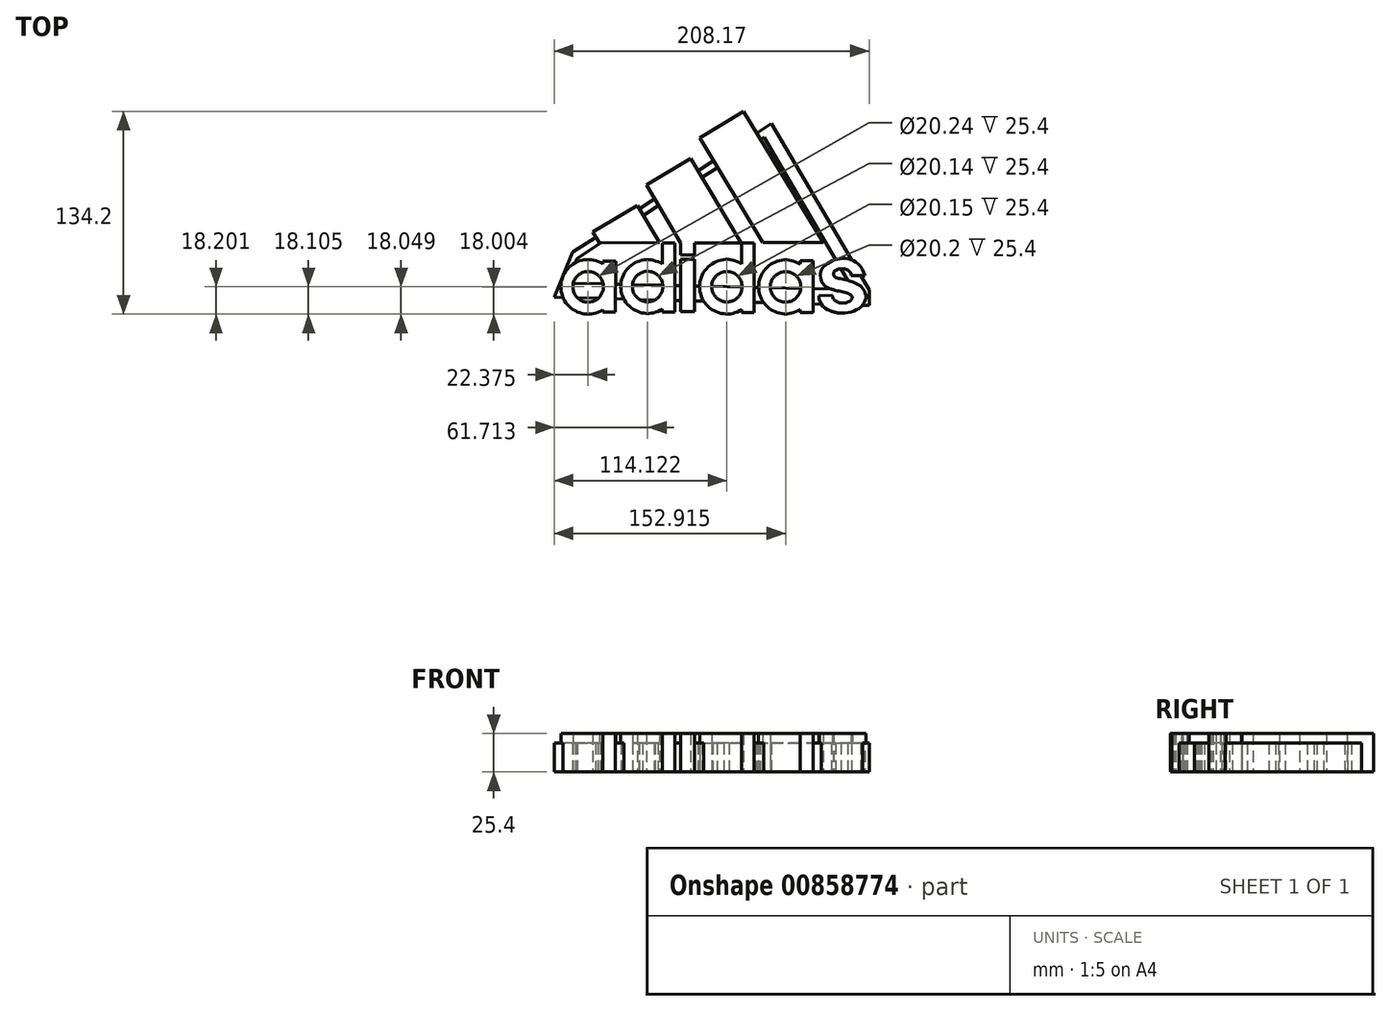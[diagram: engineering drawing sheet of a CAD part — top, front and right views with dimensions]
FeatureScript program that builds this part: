
annotation { "Feature Type Name" : "Feature", "Feature Type Description" : "" }
export const myFeature = defineFeature(function(context is Context, id is Id, definition is map)
    precondition{}
    {
        {
            var Q0;
            Q0=qCreatedBy(makeId("Top.planeOp"),FACE);
            var sketch = newSketch(context, id + "F0", { "sketchPlane" : qUnion([Q0])});
            skLineSegment(sketch, "E0", {"start": v(-108.73, -20.06) * mm, "end": v(-104.25, -27.54) * mm});
            skLineSegment(sketch, "E1", {"start": v(-64.76, -27.2) * mm, "end": v(-104.25, -27.54) * mm});
            skLineSegment(sketch, "E2", {"start": v(-108.73, -20.06) * mm, "end": v(-79.42, -2.53) * mm});
            skLineSegment(sketch, "E3", {"start": v(-79.42, -2.53) * mm, "end": v(-64.76, -27.2) * mm});
            skLineSegment(sketch, "E4", {"start": v(-73.41, 10.93) * mm, "end": v(-50.58, -27.49) * mm});
            skLineSegment(sketch, "E5", {"start": v(-50.58, -27.49) * mm, "end": v(-10.72, -27.49) * mm});
            skLineSegment(sketch, "E6", {"start": v(-10.72, -27.49) * mm, "end": v(-43.97, 28.43) * mm});
            skLineSegment(sketch, "E7", {"start": v(-43.97, 28.43) * mm, "end": v(-73.41, 10.93) * mm});
            skLineSegment(sketch, "E8", {"start": v(-38.16, 42.1) * mm, "end": v(3.67, -27.23) * mm});
            skLineSegment(sketch, "E9", {"start": v(-38.16, 42.1) * mm, "end": v(-8.99, 59.7) * mm});
            skLineSegment(sketch, "E10", {"start": v(-8.99, 59.7) * mm, "end": v(43.48, -27.26) * mm});
            skLineSegment(sketch, "E11", {"start": v(43.48, -27.26) * mm, "end": v(3.67, -27.23) * mm});
            skCircle(sketch, "E12", {"center": v(-111.85, -56.45) * mm, "radius": 10.12 * mm});
            skCircle(sketch, "E13", {"center": v(-111.85, -56.45) * mm, "radius": 18.05 * mm});
            skLineSegment(sketch, "E14", {"start": v(-102.06, -39.5) * mm, "end": v(-102.06, -73.1) * mm});
            skLineSegment(sketch, "E15", {"start": v(-102.06, -73.1) * mm, "end": v(-93.82, -73.1) * mm});
            skLineSegment(sketch, "E16", {"start": v(-102.06, -39.5) * mm, "end": v(-93.69, -39.5) * mm});
            skLineSegment(sketch, "E17", {"start": v(-93.69, -39.5) * mm, "end": v(-93.82, -73.1) * mm});
            skLineSegment(sketch, "E18.bottom", {"start": v(-62.74, -27.53) * mm, "end": v(-54.5, -27.53) * mm});
            skLineSegment(sketch, "E18.top", {"start": v(-62.74, -73.26) * mm, "end": v(-54.5, -73.26) * mm});
            skLineSegment(sketch, "E18.left", {"start": v(-62.74, -27.53) * mm, "end": v(-62.74, -73.26) * mm});
            skLineSegment(sketch, "E18.right", {"start": v(-54.5, -27.53) * mm, "end": v(-54.5, -73.26) * mm});
            skCircle(sketch, "E19", {"center": v(-72.52, -56.3) * mm, "radius": 10.07 * mm});
            skPoint(sketch, "E19.centerSnap0", {"position": v(-93.76, -56.3) * mm});
            skCircle(sketch, "E20", {"center": v(-72.52, -56.3) * mm, "radius": 17.78 * mm});
            skLineSegment(sketch, "E21.bottom", {"start": v(-41.5, -35.39) * mm, "end": v(-50.58, -35.39) * mm});
            skLineSegment(sketch, "E21.top", {"start": v(-41.5, -27.49) * mm, "end": v(-50.58, -27.49) * mm});
            skLineSegment(sketch, "E21.left", {"start": v(-41.5, -35.39) * mm, "end": v(-41.5, -27.49) * mm});
            skLineSegment(sketch, "E21.right", {"start": v(-50.58, -35.39) * mm, "end": v(-50.58, -27.49) * mm});
            skLineSegment(sketch, "E22.bottom", {"start": v(-41.5, -72.88) * mm, "end": v(-50.58, -72.88) * mm});
            skLineSegment(sketch, "E22.top", {"start": v(-41.5, -38.2) * mm, "end": v(-50.58, -38.2) * mm});
            skLineSegment(sketch, "E22.left", {"start": v(-41.5, -72.88) * mm, "end": v(-41.5, -38.2) * mm});
            skLineSegment(sketch, "E22.right", {"start": v(-50.58, -72.88) * mm, "end": v(-50.58, -38.2) * mm});
            skCircle(sketch, "E23", {"center": v(-20.1, -56.4) * mm, "radius": 10.07 * mm});
            skCircle(sketch, "E24", {"center": v(-20.1, -56.4) * mm, "radius": 18.03 * mm});
            skLineSegment(sketch, "E25.bottom", {"start": v(-2.09, -27.49) * mm, "end": v(-10.23, -27.49) * mm});
            skLineSegment(sketch, "E25.top", {"start": v(-2.09, -73.45) * mm, "end": v(-10.23, -73.45) * mm});
            skLineSegment(sketch, "E25.left", {"start": v(-2.09, -27.49) * mm, "end": v(-2.09, -73.45) * mm});
            skLineSegment(sketch, "E25.right", {"start": v(-10.23, -27.49) * mm, "end": v(-10.23, -73.45) * mm});
            skCircle(sketch, "E26", {"center": v(18.68, -56.5) * mm, "radius": 10.1 * mm});
            skCircle(sketch, "E27", {"center": v(18.68, -56.5) * mm, "radius": 17.84 * mm});
            skLineSegment(sketch, "E28.bottom", {"start": v(36.83, -39.32) * mm, "end": v(28.43, -39.32) * mm});
            skLineSegment(sketch, "E28.top", {"start": v(36.83, -73.47) * mm, "end": v(28.43, -73.47) * mm});
            skLineSegment(sketch, "E28.left", {"start": v(36.83, -39.32) * mm, "end": v(36.83, -73.47) * mm});
            skLineSegment(sketch, "E28.right", {"start": v(28.43, -39.32) * mm, "end": v(28.43, -73.47) * mm});
            skFitSpline(sketch, "E29", {"points": [v(40.61, -62.28) * mm, v(71.7, -62.17) * mm], "startDerivative": vector(1.62, -49.72) * mm, "endDerivative": vector(-4.39, 42.82) * mm});
            skFitSpline(sketch, "E30", {"points": [v(71.7, -62.17) * mm, v(50.6, -47.52) * mm], "startDerivative": vector(-6.03, 39.02) * mm, "endDerivative": vector(7.86, 17.11) * mm});
            skFitSpline(sketch, "E31", {"points": [v(50.6, -47.52) * mm, v(62.11, -49.02) * mm], "startDerivative": vector(-5.58, 6.43) * mm, "endDerivative": vector(4.14, -23.75) * mm});
            skFitSpline(sketch, "E32", {"points": [v(71.08, -49.17) * mm, v(41.72, -49.17) * mm], "startDerivative": vector(-16, 60.18) * mm, "endDerivative": vector(5.1, -29.55) * mm});
            skFitSpline(sketch, "E33", {"points": [v(41.72, -49.17) * mm, v(62.92, -63.95) * mm], "startDerivative": vector(1.36, -39.32) * mm, "endDerivative": vector(3.01, -20.74) * mm});
            skFitSpline(sketch, "E34", {"points": [v(62.92, -63.95) * mm, v(49.69, -61.97) * mm], "startDerivative": vector(-10.24, -16.5) * mm, "endDerivative": vector(1, 16.73) * mm});
            skLineSegment(sketch, "E35", {"start": v(40.61, -62.28) * mm, "end": v(49.69, -61.97) * mm});
            skLineSegment(sketch, "E36", {"start": v(62.11, -49.02) * mm, "end": v(71.08, -49.17) * mm});
            skSolve(sketch);
        }
        {
            var Q0;
            Q0=qCreatedBy(makeId("Top.planeOp"),FACE);
            var sketch = newSketch(context, id + "F1", { "sketchPlane" : qUnion([Q0])});
            skLineSegment(sketch, "E37", {"start": v(-122.16, -33.53) * mm, "end": v(9.42, 51.78) * mm});
            skLineSegment(sketch, "E38", {"start": v(9.42, 51.78) * mm, "end": v(73.94, -58.57) * mm});
            skLineSegment(sketch, "E39", {"start": v(73.94, -58.57) * mm, "end": v(73.94, -68.76) * mm});
            skLineSegment(sketch, "E40", {"start": v(73.94, -68.76) * mm, "end": v(-134.23, -63.34) * mm});
            skLineSegment(sketch, "E41", {"start": v(-134.23, -63.34) * mm, "end": v(-122.16, -33.53) * mm});
            skLineSegment(sketch, "E42", {"start": v(-122.16, -33.53) * mm, "end": v(-119.4, -37.78) * mm});
            skLineSegment(sketch, "E43", {"start": v(-119.4, -37.78) * mm, "end": v(-128.2, -63.5) * mm});
            skPoint(sketch, "E43.endSnap0", {"position": v(-128.2, -48.44) * mm});
            skLineSegment(sketch, "E44", {"start": v(-119.4, -37.78) * mm, "end": v(11.98, 47.41) * mm});
            skLineSegment(sketch, "E45", {"start": v(73.94, -58.57) * mm, "end": v(-124.94, -53.97) * mm});
            skLineSegment(sketch, "E46", {"start": v(63.3, -58.33) * mm, "end": v(4.37, 42.48) * mm});
            skSolve(sketch);
        }
        {
            var Q0;
            Q0=makeQuery(id+"F0.imprint","IMPRINT",FACE,{"disambiguationData":[TD([[makeQuery(id+"F0.imprint","IMPRINT",EDGE,{"derivedFrom":sQuery(id+"F0.wireOp",EDGE,"E4")}),1.0]])]});
            var Q1;
            Q1=makeQuery(id+"F0.imprint","IMPRINT",FACE,{"disambiguationData":[TD([[makeQuery(id+"F0.imprint","IMPRINT",EDGE,{"derivedFrom":sQuery(id+"F0.wireOp",EDGE,"E8")}),1.0]])]});
            var Q2;
            Q2=makeQuery(id+"F0.imprint","IMPRINT",FACE,{"disambiguationData":[TD([[makeQuery(id+"F0.imprint","IMPRINT",EDGE,{"derivedFrom":sQuery(id+"F0.wireOp",EDGE,"E0")}),1.0]])]});
            var Q3;
            {var subQ0=sQuery(id+"F0.wireOp",EDGE,"E14");var subQ1=sQuery(id+"F0.wireOp",EDGE,"E12");var subQ2=makeQuery(id+"F0.imprint","INTERSECT",VERTEX,{"disambiguationData":[OD(0.0)],"derivedFrom":[subQ1,subQ0]});Q3=makeQuery(id+"F0.imprint","IMPRINT",FACE,{"disambiguationData":[TD([[makeQuery(id+"F0.imprint","IMPRINT",EDGE,{"disambiguationData":[TD([[subQ2,-1.0]])],"derivedFrom":subQ1}),-1.0]])]});}
            var Q4;
            {var subQ0=sQuery(id+"F0.wireOp",EDGE,"E14");var subQ1=sQuery(id+"F0.wireOp",EDGE,"E12");var subQ2=makeQuery(id+"F0.imprint","INTERSECT",VERTEX,{"disambiguationData":[OD(0.0)],"derivedFrom":[subQ1,subQ0]});Q4=makeQuery(id+"F0.imprint","IMPRINT",FACE,{"disambiguationData":[TD([[makeQuery(id+"F0.imprint","IMPRINT",EDGE,{"disambiguationData":[TD([[subQ2,1.0]])],"derivedFrom":subQ1}),-1.0]])]});}
            var Q5;
            {var subQ0=sQuery(id+"F0.wireOp",EDGE,"E20");var subQ1=sQuery(id+"F0.wireOp",EDGE,"E18.left");var subQ2=makeQuery(id+"F0.imprint","INTERSECT",VERTEX,{"disambiguationData":[OD(0.0)],"derivedFrom":[subQ1,subQ0]});Q5=makeQuery(id+"F0.imprint","IMPRINT",FACE,{"disambiguationData":[TD([[makeQuery(id+"F0.imprint","IMPRINT",EDGE,{"disambiguationData":[TD([[subQ2,-1.0]])],"derivedFrom":subQ1}),1.0]])]});}
            var Q6;
            {var subQ0=sQuery(id+"F0.wireOp",EDGE,"E20");var subQ1=sQuery(id+"F0.wireOp",EDGE,"E18.left");var subQ2=makeQuery(id+"F0.imprint","INTERSECT",VERTEX,{"disambiguationData":[OD(0.0)],"derivedFrom":[subQ1,subQ0]});Q6=makeQuery(id+"F0.imprint","IMPRINT",FACE,{"disambiguationData":[TD([[makeQuery(id+"F0.imprint","IMPRINT",EDGE,{"disambiguationData":[TD([[subQ2,-1.0]])],"derivedFrom":subQ1}),-1.0]])]});}
            var Q7;
            {var subQ1=sQuery(id+"F0.wireOp",EDGE,"E18.bottom");Q7=makeQuery(id+"F0.imprint","IMPRINT",FACE,{"disambiguationData":[TD([[makeQuery(id+"F0.imprint","IMPRINT",EDGE,{"derivedFrom":subQ1}),-1.0]])]});}
            var Q8;
            Q8=makeQuery(id+"F0.imprint","IMPRINT",FACE,{"disambiguationData":[TD([[makeQuery(id+"F0.imprint","IMPRINT",EDGE,{"derivedFrom":sQuery(id+"F0.wireOp",EDGE,"E22.bottom")}),-1.0]])]});
            var Q9;
            Q9=makeQuery(id+"F0.imprint","IMPRINT",FACE,{"disambiguationData":[TD([[makeQuery(id+"F0.imprint","IMPRINT",EDGE,{"derivedFrom":sQuery(id+"F0.wireOp",EDGE,"E21.bottom")}),-1.0]])]});
            var Q10;
            {var subQ0=sQuery(id+"F0.wireOp",EDGE,"E25.right");var subQ1=sQuery(id+"F0.wireOp",EDGE,"E23");var subQ2=makeQuery(id+"F0.imprint","INTERSECT",VERTEX,{"disambiguationData":[OD(0.0)],"derivedFrom":[subQ1,subQ0]});Q10=makeQuery(id+"F0.imprint","IMPRINT",FACE,{"disambiguationData":[TD([[makeQuery(id+"F0.imprint","IMPRINT",EDGE,{"disambiguationData":[TD([[subQ2,-1.0]])],"derivedFrom":subQ1}),-1.0]])]});}
            var Q11;
            {var subQ4=sQuery(id+"F0.wireOp",EDGE,"E25.right");var subQ7=sQuery(id+"F0.wireOp",EDGE,"E23");var subQ8=makeQuery(id+"F0.imprint","INTERSECT",VERTEX,{"disambiguationData":[OD(0.0)],"derivedFrom":[subQ7,subQ4]});Q11=makeQuery(id+"F0.imprint","IMPRINT",FACE,{"disambiguationData":[TD([[makeQuery(id+"F0.imprint","IMPRINT",EDGE,{"disambiguationData":[TD([[subQ8,1.0]])],"derivedFrom":subQ7}),-1.0]])]});}
            var Q12;
            {var subQ5=sQuery(id+"F0.wireOp",EDGE,"E25.bottom");Q12=makeQuery(id+"F0.imprint","IMPRINT",FACE,{"disambiguationData":[TD([[makeQuery(id+"F0.imprint","IMPRINT",EDGE,{"derivedFrom":subQ5}),1.0]])]});}
            var Q13;
            {var subQ5=sQuery(id+"F0.wireOp",EDGE,"E25.top");Q13=makeQuery(id+"F0.imprint","IMPRINT",FACE,{"disambiguationData":[TD([[makeQuery(id+"F0.imprint","IMPRINT",EDGE,{"derivedFrom":subQ5}),-1.0]])]});}
            var Q14;
            {var subQ0=sQuery(id+"F0.wireOp",EDGE,"E28.right");var subQ1=sQuery(id+"F0.wireOp",EDGE,"E26");var subQ2=makeQuery(id+"F0.imprint","INTERSECT",VERTEX,{"disambiguationData":[OD(0.0)],"derivedFrom":[subQ1,subQ0]});Q14=makeQuery(id+"F0.imprint","IMPRINT",FACE,{"disambiguationData":[TD([[makeQuery(id+"F0.imprint","IMPRINT",EDGE,{"disambiguationData":[TD([[subQ2,-1.0]])],"derivedFrom":subQ1}),-1.0]])]});}
            var Q15;
            {var subQ0=sQuery(id+"F0.wireOp",EDGE,"E28.right");var subQ1=sQuery(id+"F0.wireOp",EDGE,"E26");var subQ2=makeQuery(id+"F0.imprint","INTERSECT",VERTEX,{"disambiguationData":[OD(0.0)],"derivedFrom":[subQ1,subQ0]});Q15=makeQuery(id+"F0.imprint","IMPRINT",FACE,{"disambiguationData":[TD([[makeQuery(id+"F0.imprint","IMPRINT",EDGE,{"disambiguationData":[TD([[subQ2,1.0]])],"derivedFrom":subQ1}),-1.0]])]});}
            var Q16;
            {var subQ1=sQuery(id+"F0.wireOp",EDGE,"E28.bottom");Q16=makeQuery(id+"F0.imprint","IMPRINT",FACE,{"disambiguationData":[TD([[makeQuery(id+"F0.imprint","IMPRINT",EDGE,{"derivedFrom":subQ1}),1.0]])]});}
            var Q17;
            Q17=makeQuery(id+"F0.imprint","IMPRINT",FACE,{"disambiguationData":[TD([[makeQuery(id+"F0.imprint","IMPRINT",EDGE,{"derivedFrom":sQuery(id+"F0.wireOp",EDGE,"E29")}),1.0]])]});
            var Q18;
            {var subQ0=sQuery(id+"F0.wireOp",EDGE,"E15");Q18=makeQuery(id+"F0.imprint","IMPRINT",FACE,{"disambiguationData":[TD([[makeQuery(id+"F0.imprint","IMPRINT",EDGE,{"derivedFrom":subQ0}),1.0]])]});}
            extrude(context, id + "F2", {"entities" : qUnion([Q0, Q1, Q2, Q3, Q4, Q5, Q6, Q7, Q8, Q9, Q10, Q11, Q12, Q13, Q14, Q15, Q16, Q17, Q18]), "depth" : 25.4 * mm, "offsetDistance" : 25.4 * mm});
        }
        {
            var Q0;
            {var subQ5=sQuery(id+"F1.wireOp",EDGE,"E46");Q0=makeQuery(id+"F1.imprint","IMPRINT",FACE,{"disambiguationData":[TD([[makeQuery(id+"F1.imprint","IMPRINT",EDGE,{"derivedFrom":subQ5}),-1.0]])]});}
            var Q1;
            {var subQ2=sQuery(id+"F1.wireOp",EDGE,"E37");Q1=makeQuery(id+"F1.imprint","IMPRINT",FACE,{"disambiguationData":[TD([[makeQuery(id+"F1.imprint","IMPRINT",EDGE,{"derivedFrom":subQ2}),-1.0]])]});}
            var Q2;
            {var subQ1=sQuery(id+"F1.wireOp",EDGE,"E39");Q2=makeQuery(id+"F1.imprint","IMPRINT",FACE,{"disambiguationData":[TD([[makeQuery(id+"F1.imprint","IMPRINT",EDGE,{"derivedFrom":subQ1}),-1.0]])]});}
            var Q3;
            {var subQ3=sQuery(id+"F1.wireOp",EDGE,"E41");Q3=makeQuery(id+"F1.imprint","IMPRINT",FACE,{"disambiguationData":[TD([[makeQuery(id+"F1.imprint","IMPRINT",EDGE,{"derivedFrom":subQ3}),-1.0]])]});}
            extrude(context, id + "F3", {"entities" : qUnion([Q0, Q1, Q2, Q3]), "operationType" : NewBodyOperationType.ADD, "depth" : 19.05 * mm, "offsetDistance" : 25.4 * mm});
        }
    });
